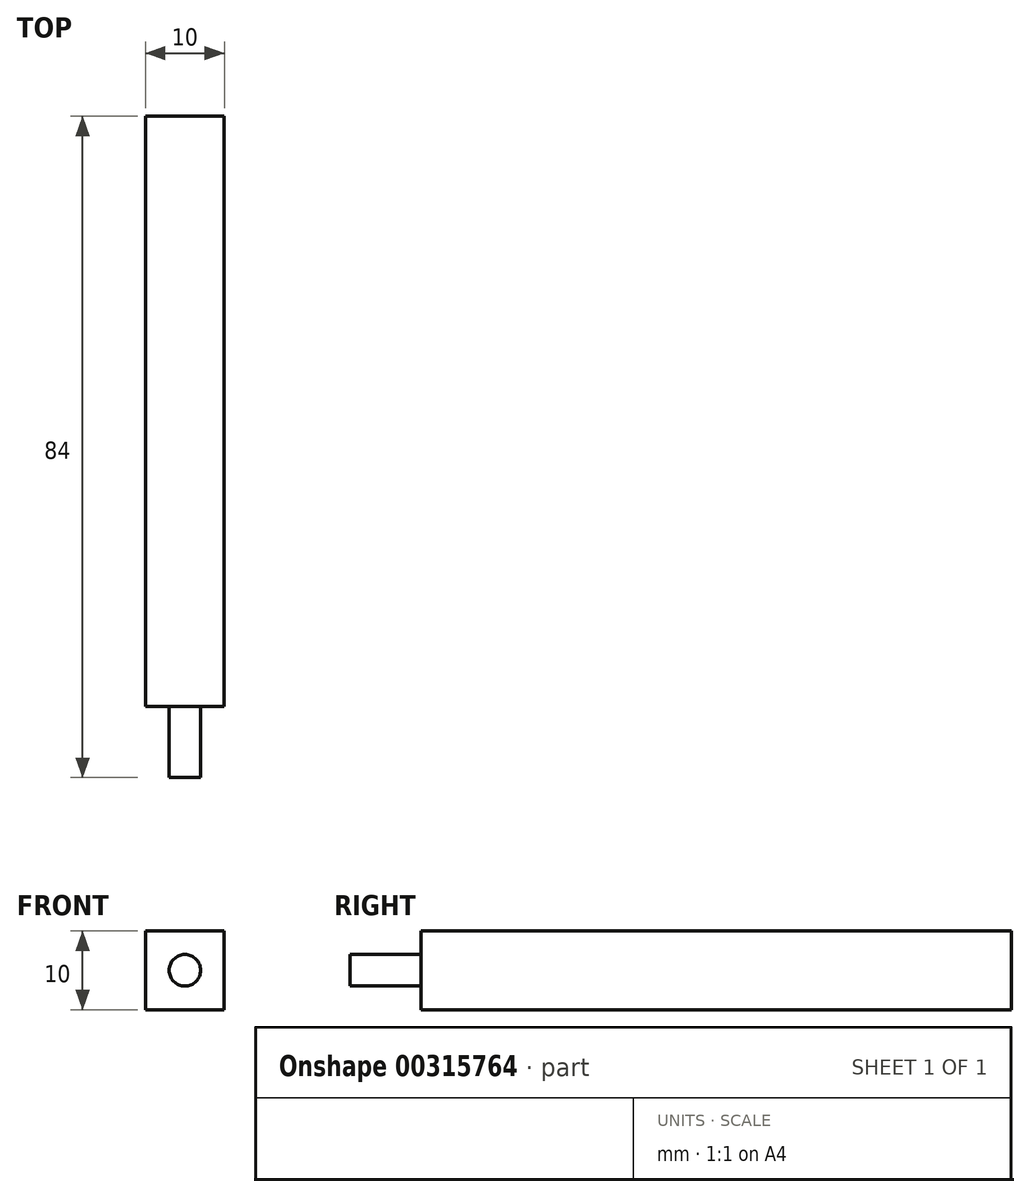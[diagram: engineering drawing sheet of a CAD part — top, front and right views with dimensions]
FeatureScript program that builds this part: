
annotation { "Feature Type Name" : "Feature", "Feature Type Description" : "" }
export const myFeature = defineFeature(function(context is Context, id is Id, definition is map)
    precondition{}
    {
        {
            var Q0;
            Q0=qCreatedBy(makeId("Front.planeOp"),FACE);
            var sketch = newSketch(context, id + "F0", { "sketchPlane" : qUnion([Q0])});
            skLineSegment(sketch, "E0.bottom", {"start": v(-5, 5) * mm, "end": v(5, 5) * mm});
            skLineSegment(sketch, "E0.top", {"start": v(-5, -5) * mm, "end": v(5, -5) * mm});
            skLineSegment(sketch, "E0.left", {"start": v(-5, 5) * mm, "end": v(-5, -5) * mm});
            skLineSegment(sketch, "E0.right", {"start": v(5, 5) * mm, "end": v(5, -5) * mm});
            skPoint(sketch, "E1", {"position": v(0, 5) * mm});
            skPoint(sketch, "E2", {"position": v(0, -5) * mm});
            skSolve(sketch);
        }
        {
            var Q0;
            Q0=makeQuery(id+"F0.imprint","IMPRINT",FACE,{"disambiguationData":[TD([[makeQuery(id+"F0.imprint","IMPRINT",EDGE,{"derivedFrom":sQuery(id+"F0.wireOp",EDGE,"E0.bottom")}),-1.0]])]});
            extrude(context, id + "F1", {"entities" : qUnion([Q0]), "depth" : 75 * mm});
        }
        {
            var Q0;
            Q0=makeQuery(id+"F1.opExtrude","CAP_FACE",FACE,{"disambiguationData":[OSD([sQuery(id+"F0.wireOp",EDGE,"E0.bottom"),sQuery(id+"F0.wireOp",EDGE,"E0.top"),sQuery(id+"F0.wireOp",EDGE,"E0.left"),sQuery(id+"F0.wireOp",EDGE,"E0.right")])],"isStart":false});
            var sketch = newSketch(context, id + "F2", { "sketchPlane" : qUnion([Q0])});
            skPoint(sketch, "E3", {"position": v(0, 5) * mm});
            skPoint(sketch, "E4", {"position": v(0, 0) * mm});
            skCircle(sketch, "E5", {"center": v(0, 0) * mm, "radius": 2 * mm});
            skSolve(sketch);
        }
        {
            var Q0;
            Q0=makeQuery(id+"F2.imprint","IMPRINT",FACE,{"disambiguationData":[TD([[makeQuery(id+"F2.imprint","IMPRINT",EDGE,{"derivedFrom":sQuery(id+"F2.wireOp",EDGE,"E5")}),1.0]])]});
            extrude(context, id + "F3", {"entities" : qUnion([Q0]), "operationType" : NewBodyOperationType.ADD, "depth" : 9 * mm});
        }
    });
